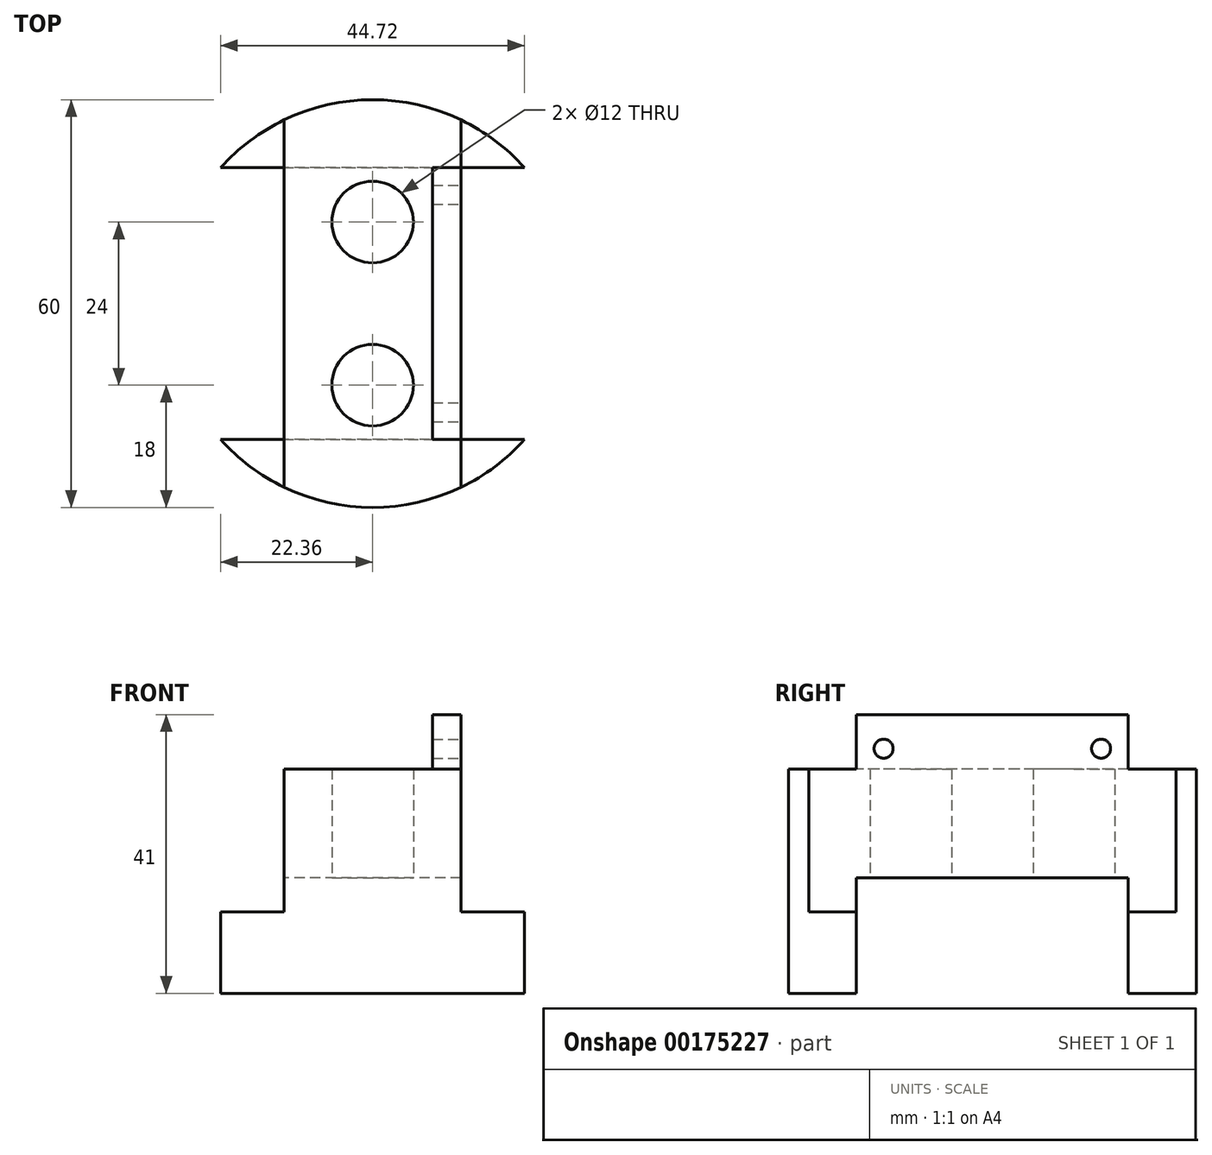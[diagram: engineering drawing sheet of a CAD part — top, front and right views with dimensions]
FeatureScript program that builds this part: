
annotation { "Feature Type Name" : "Feature", "Feature Type Description" : "" }
export const myFeature = defineFeature(function(context is Context, id is Id, definition is map)
    precondition{}
    {
        {
            var Q0;
            Q0=qCreatedBy(makeId("Top.planeOp"),FACE);
            var sketch = newSketch(context, id + "F0", { "sketchPlane" : qUnion([Q0])});
            skLineSegment(sketch, "E0.bottom", {"start": v(-13, -12) * mm, "end": v(13, -12) * mm});
            skLineSegment(sketch, "E0.top", {"start": v(-13, 12) * mm, "end": v(13, 12) * mm});
            skLineSegment(sketch, "E0.left", {"start": v(-13, -12) * mm, "end": v(-13, 12) * mm});
            skLineSegment(sketch, "E0.right", {"start": v(13, -12) * mm, "end": v(13, 12) * mm});
            skPoint(sketch, "E0.middle", {"position": v(0, 0) * mm});
            skCircle(sketch, "E1", {"center": v(0, 0) * mm, "radius": 20 * mm, "construction": true});
            skLineSegment(sketch, "E2", {"start": v(-31.1, 0) * mm, "end": v(39.02, 0) * mm, "construction": true});
            skCircle(sketch, "E3", {"center": v(0, 0) * mm, "radius": 30 * mm});
            skCircle(sketch, "E4", {"center": v(0, 12) * mm, "radius": 6 * mm});
            skCircle(sketch, "E5", {"center": v(0, -12) * mm, "radius": 6 * mm});
            skLineSegment(sketch, "E6.bottom", {"start": v(-13, 27.04) * mm, "end": v(13, 27.04) * mm});
            skLineSegment(sketch, "E6.top", {"start": v(-13, -27.04) * mm, "end": v(13, -27.04) * mm});
            skLineSegment(sketch, "E6.left", {"start": v(-13, 27.04) * mm, "end": v(-13, -27.04) * mm});
            skLineSegment(sketch, "E6.right", {"start": v(13, 27.04) * mm, "end": v(13, -27.04) * mm});
            skSolve(sketch);
        }
        {
            var Q0;
            {var subQ0=sQuery(id+"F0.wireOp",EDGE,"E6.bottom");Q0=makeQuery(id+"F0.imprint","IMPRINT",FACE,{"disambiguationData":[TD([[makeQuery(id+"F0.imprint","IMPRINT",EDGE,{"derivedFrom":subQ0}),1.0]])]});}
            var Q1;
            {var subQ0=sQuery(id+"F0.wireOp",EDGE,"E6.top");Q1=makeQuery(id+"F0.imprint","IMPRINT",FACE,{"disambiguationData":[TD([[makeQuery(id+"F0.imprint","IMPRINT",EDGE,{"derivedFrom":subQ0}),-1.0]])]});}
            var Q2;
            {var subQ0=sQuery(id+"F0.wireOp",EDGE,"E6.top");Q2=makeQuery(id+"F0.imprint","IMPRINT",FACE,{"disambiguationData":[TD([[makeQuery(id+"F0.imprint","IMPRINT",EDGE,{"derivedFrom":subQ0}),1.0]])]});}
            var Q3;
            {var subQ6=sQuery(id+"F0.wireOp",EDGE,"E0.bottom");var subQ9=sQuery(id+"F0.wireOp",EDGE,"E6.left");var subQ13=makeQuery(id+"F0.imprint","INTERSECT",VERTEX,{"derivedFrom":[subQ6,subQ9]});Q3=makeQuery(id+"F0.imprint","IMPRINT",FACE,{"disambiguationData":[TD([[makeQuery(id+"F0.imprint","IMPRINT",EDGE,{"disambiguationData":[TD([[subQ13,-1.0]])],"derivedFrom":subQ6}),1.0]])]});}
            var Q4;
            {var subQ0=sQuery(id+"F0.wireOp",EDGE,"E6.bottom");Q4=makeQuery(id+"F0.imprint","IMPRINT",FACE,{"disambiguationData":[TD([[makeQuery(id+"F0.imprint","IMPRINT",EDGE,{"derivedFrom":subQ0}),-1.0]])]});}
            extrude(context, id + "F1", {"entities" : qUnion([Q0, Q1, Q2, Q3, Q4]), "depth" : 33 * mm});
        }
        {
            var Q0;
            Q0=qCreatedBy(makeId("Top.planeOp"),FACE);
            var sketch = newSketch(context, id + "F2", { "sketchPlane" : qUnion([Q0])});
            skCircle(sketch, "E7", {"center": v(0, 0) * mm, "radius": 30 * mm});
            skCircle(sketch, "E8", {"center": v(-26.68, -13.72) * mm, "radius": 7.63 * mm});
            skLineSegment(sketch, "E9", {"start": v(-22.36, -20) * mm, "end": v(-12.88, -20) * mm});
            skLineSegment(sketch, "E10", {"start": v(-12.88, -20) * mm, "end": v(22.36, -20) * mm});
            skLineSegment(sketch, "E11", {"start": v(22.36, -20) * mm, "end": v(-53.5, 0) * mm, "construction": true});
            skLineSegment(sketch, "E12", {"start": v(-53.5, 0) * mm, "end": v(57.64, 0) * mm, "construction": true});
            skLineSegment(sketch, "E13.MirrorCS", {"start": v(-12.88, 20) * mm, "end": v(22.36, 20) * mm});
            skLineSegment(sketch, "E14.MirrorCS", {"start": v(-22.36, 20) * mm, "end": v(-12.88, 20) * mm});
            skSolve(sketch);
        }
        {
            var Q0;
            {var subQ0=sQuery(id+"F2.wireOp",EDGE,"E13.MirrorCS");Q0=makeQuery(id+"F2.imprint","IMPRINT",FACE,{"disambiguationData":[TD([[makeQuery(id+"F2.imprint","IMPRINT",EDGE,{"derivedFrom":subQ0}),1.0]])]});}
            var Q1;
            {var subQ0=sQuery(id+"F2.wireOp",EDGE,"E9");Q1=makeQuery(id+"F2.imprint","IMPRINT",FACE,{"disambiguationData":[TD([[makeQuery(id+"F2.imprint","IMPRINT",EDGE,{"derivedFrom":subQ0}),-1.0]])]});}
            extrude(context, id + "F3", {"entities" : qUnion([Q0, Q1]), "operationType" : NewBodyOperationType.ADD, "depth" : 12 * mm});
        }
        {
            var Q0;
            Q0=makeQuery(id+"F1.opExtrude","CAP_FACE",FACE,{"disambiguationData":[OSD([sQuery(id+"F0.wireOp",EDGE,"E3"),sQuery(id+"F0.wireOp",EDGE,"E4"),sQuery(id+"F0.wireOp",EDGE,"E5"),sQuery(id+"F0.wireOp",EDGE,"E6.left"),sQuery(id+"F0.wireOp",EDGE,"E6.right")])],"isStart":false});
            var sketch = newSketch(context, id + "F4", { "sketchPlane" : qUnion([Q0])});
            skLineSegment(sketch, "E15", {"start": v(0, 35.89) * mm, "end": v(0, -37.95) * mm});
            skPoint(sketch, "E15.endSnap0", {"position": v(0, 30) * mm});
            skLineSegment(sketch, "E16", {"start": v(0, -37.95) * mm, "end": v(28.6, -37.95) * mm});
            skLineSegment(sketch, "E17", {"start": v(28.6, -37.95) * mm, "end": v(28.6, 36.6) * mm});
            skLineSegment(sketch, "E18", {"start": v(28.6, 36.6) * mm, "end": v(0, 36.6) * mm});
            skLineSegment(sketch, "E19", {"start": v(0, 36.6) * mm, "end": v(0, 33.04) * mm});
            skSolve(sketch);
        }
        {
            var Q0;
            Q0=makeQuery(id+"F1.opExtrude","SWEPT_FACE",FACE,{"disambiguationData":[OSD([sQuery(id+"F0.wireOp",EDGE,"E6.left")])]});
            var sketch = newSketch(context, id + "F5", { "sketchPlane" : qUnion([Q0])});
            skLineSegment(sketch, "E20.bottom", {"start": v(-20, 0) * mm, "end": v(20, 0) * mm});
            skLineSegment(sketch, "E20.top", {"start": v(-20, 17) * mm, "end": v(20, 17) * mm});
            skLineSegment(sketch, "E20.left", {"start": v(-20, 0) * mm, "end": v(-20, 17) * mm});
            skLineSegment(sketch, "E20.right", {"start": v(20, 0) * mm, "end": v(20, 17) * mm});
            skSolve(sketch);
        }
        {
            var Q0;
            {var subQ5=sQuery(id+"F5.wireOp",EDGE,"E20.bottom");Q0=makeQuery(id+"F5.imprint","IMPRINT",FACE,{"disambiguationData":[TD([[makeQuery(id+"F5.imprint","IMPRINT",EDGE,{"derivedFrom":subQ5}),1.0]])]});}
            extrude(context, id + "F6", {"entities" : qUnion([Q0]), "operationType" : NewBodyOperationType.REMOVE, "endBound" : BoundingType.THROUGH_ALL, "oppositeDirection" : true, "depth" : 25 * mm});
        }
        {
            var Q0;
            Q0=makeQuery(id+"F6.boolean.opBoolean","COPY",FACE,{"derivedFrom":makeQuery(id+"F6.opExtrude","SWEPT_FACE",FACE,{"disambiguationData":[OSD([sQuery(id+"F5.wireOp",EDGE,"E20.top")])]})});
            var sketch = newSketch(context, id + "F7", { "sketchPlane" : qUnion([Q0])});
            skCircle(sketch, "E21", {"center": v(0, 12) * mm, "radius": 11.29 * mm, "construction": true});
            skCircle(sketch, "E22", {"center": v(0, -12) * mm, "radius": 11.29 * mm, "construction": true});
            skCircle(sketch, "E23", {"center": v(0, 12) * mm, "radius": 11.29 * mm});
            skCircle(sketch, "E24", {"center": v(0, -12) * mm, "radius": 11.29 * mm});
            skSolve(sketch);
        }
        {
            var Q0;
            Q0=makeQuery(id+"F7.imprint","IMPRINT",FACE,{"disambiguationData":[TD([[makeQuery(id+"F7.imprint","IMPRINT",EDGE,{"derivedFrom":makeQuery(id+"F6.boolean.opBoolean","INTERSECT",EDGE,{"derivedFrom":[makeQuery(id+"F1.opExtrude","SWEPT_FACE",FACE,{"disambiguationData":[OSD([sQuery(id+"F0.wireOp",EDGE,"E4")])]}),makeQuery(id+"F6.opExtrude","SWEPT_FACE",FACE,{"disambiguationData":[OSD([sQuery(id+"F5.wireOp",EDGE,"E20.top")])]})]})}),1.0]])]});
            var Q1;
            Q1=makeQuery(id+"F7.imprint","IMPRINT",FACE,{"disambiguationData":[TD([[makeQuery(id+"F7.imprint","IMPRINT",EDGE,{"derivedFrom":makeQuery(id+"F6.boolean.opBoolean","INTERSECT",EDGE,{"derivedFrom":[makeQuery(id+"F1.opExtrude","SWEPT_FACE",FACE,{"disambiguationData":[OSD([sQuery(id+"F0.wireOp",EDGE,"E5")])]}),makeQuery(id+"F6.opExtrude","SWEPT_FACE",FACE,{"disambiguationData":[OSD([sQuery(id+"F5.wireOp",EDGE,"E20.top")])]})]})}),1.0]])]});
            var Q2;
            {var subQ0=sQuery(id+"F7.wireOp",EDGE,"E23");var subQ1=makeQuery(id+"F6.boolean.opBoolean","COPY",EDGE,{"derivedFrom":makeQuery(id+"F6.opExtrude","SWEPT_EDGE",EDGE,{"disambiguationData":[OSD([sQuery(id+"F5.wireOp",EDGE,"E20.top"),sQuery(id+"F5.wireOp",EDGE,"E20.right")])]})});var subQ2=makeQuery(id+"F7.imprint","INTERSECT",VERTEX,{"disambiguationData":[OD(0.0)],"derivedFrom":[subQ1,subQ0]});Q2=makeQuery(id+"F7.imprint","IMPRINT",FACE,{"disambiguationData":[TD([[makeQuery(id+"F7.imprint","IMPRINT",EDGE,{"disambiguationData":[TD([[subQ2,1.0]])],"derivedFrom":subQ0}),1.0]])]});}
            var Q3;
            {var subQ0=sQuery(id+"F7.wireOp",EDGE,"E24");var subQ1=makeQuery(id+"F6.boolean.opBoolean","COPY",EDGE,{"derivedFrom":makeQuery(id+"F6.opExtrude","SWEPT_EDGE",EDGE,{"disambiguationData":[OSD([sQuery(id+"F5.wireOp",EDGE,"E20.top"),sQuery(id+"F5.wireOp",EDGE,"E20.left")])]})});var subQ2=makeQuery(id+"F7.imprint","INTERSECT",VERTEX,{"disambiguationData":[OD(0.0)],"derivedFrom":[subQ1,subQ0]});Q3=makeQuery(id+"F7.imprint","IMPRINT",FACE,{"disambiguationData":[TD([[makeQuery(id+"F7.imprint","IMPRINT",EDGE,{"disambiguationData":[TD([[subQ2,-1.0]])],"derivedFrom":subQ0}),1.0]])]});}
            var Q4;
            {var subQ1=sQuery(id+"F5.wireOp",EDGE,"E20.top");Q4=makeQuery(id+"F7.imprint","IMPRINT",FACE,{"disambiguationData":[TD([[makeQuery(id+"F7.imprint","IMPRINT",EDGE,{"derivedFrom":makeQuery(id+"F6.boolean.opBoolean","INTERSECT",EDGE,{"derivedFrom":[makeQuery(id+"F1.opExtrude","SWEPT_FACE",FACE,{"disambiguationData":[OSD([sQuery(id+"F0.wireOp",EDGE,"E5")])]}),makeQuery(id+"F6.opExtrude","SWEPT_FACE",FACE,{"disambiguationData":[OSD([subQ1])]})]})}),-1.0]])]});}
            extrude(context, id + "F8", {"entities" : qUnion([Q0, Q1, Q2, Q3, Q4]), "operationType" : NewBodyOperationType.REMOVE, "endBound" : BoundingType.THROUGH_ALL, "depth" : 25 * mm});
        }
        {
            var Q0;
            {var subQ0=sQuery(id+"F0.wireOp",EDGE,"E6.right");var subQ1=makeQuery(id+"F1.opExtrude","CAP_EDGE",EDGE,{"disambiguationData":[OSD([subQ0])],"isStart":false});Q0=makeQuery(id+"F4.imprint","IMPRINT",FACE,{"disambiguationData":[TD([[makeQuery(id+"F4.imprint","IMPRINT",EDGE,{"derivedFrom":subQ1}),-1.0]])]});}
            var sketch = newSketch(context, id + "F9", { "sketchPlane" : qUnion([Q0])});
            skLineSegment(sketch, "E25.bottom", {"start": v(13, 20) * mm, "end": v(-13, 20) * mm});
            skLineSegment(sketch, "E25.top", {"start": v(13, -20) * mm, "end": v(-13, -20) * mm});
            skLineSegment(sketch, "E25.left", {"start": v(13, 20) * mm, "end": v(13, -20) * mm});
            skLineSegment(sketch, "E25.right", {"start": v(-13, 20) * mm, "end": v(-13, -20) * mm});
            skPoint(sketch, "E25.middle", {"position": v(0, 0) * mm});
            skLineSegment(sketch, "E26.bottom", {"start": v(8.83, 20) * mm, "end": v(17.17, 20) * mm});
            skLineSegment(sketch, "E26.top", {"start": v(8.83, -20) * mm, "end": v(17.17, -20) * mm});
            skLineSegment(sketch, "E26.left", {"start": v(8.83, 20) * mm, "end": v(8.83, -20) * mm});
            skLineSegment(sketch, "E26.right", {"start": v(17.17, 20) * mm, "end": v(17.17, -20) * mm});
            skPoint(sketch, "E26.middle", {"position": v(13, 0) * mm});
            skSolve(sketch);
        }
        {
            var Q0;
            {var subQ0=sQuery(id+"F9.wireOp",EDGE,"E26.left");Q0=makeQuery(id+"F9.imprint","IMPRINT",FACE,{"disambiguationData":[TD([[makeQuery(id+"F9.imprint","IMPRINT",EDGE,{"derivedFrom":subQ0}),1.0]])]});}
            extrude(context, id + "F10", {"entities" : qUnion([Q0]), "operationType" : NewBodyOperationType.ADD, "depth" : 8 * mm});
        }
        {
            var Q0;
            {var subQ0=sQuery(id+"F0.wireOp",EDGE,"E6.right");Q0=makeQuery(id+"F10.boolean.opBoolean","MERGE",FACE,{"derivedFrom":[makeQuery(id+"F1.opExtrude","SWEPT_FACE",FACE,{"disambiguationData":[OSD([subQ0])]}),makeQuery(id+"F10.opExtrude","SWEPT_FACE",FACE,{"disambiguationData":[OSD([subQ0])]})]});}
            var sketch = newSketch(context, id + "F11", { "sketchPlane" : qUnion([Q0])});
            skLineSegment(sketch, "E27.bottom", {"start": v(-20, 41) * mm, "end": v(20, 41) * mm});
            skLineSegment(sketch, "E27.top", {"start": v(-20, 0) * mm, "end": v(20, 0) * mm});
            skLineSegment(sketch, "E27.left", {"start": v(-20, 41) * mm, "end": v(-20, 0) * mm});
            skLineSegment(sketch, "E27.right", {"start": v(20, 41) * mm, "end": v(20, 0) * mm});
            skLineSegment(sketch, "E28", {"start": v(-20, 36) * mm, "end": v(20, 36) * mm, "construction": true});
            skCircle(sketch, "E29", {"center": v(-16, 36) * mm, "radius": 1.4 * mm});
            skCircle(sketch, "E30", {"center": v(16, 36) * mm, "radius": 1.4 * mm});
            skSolve(sketch);
        }
        {
            var Q0;
            Q0=makeQuery(id+"F11.imprint","IMPRINT",FACE,{"disambiguationData":[TD([[makeQuery(id+"F11.imprint","IMPRINT",EDGE,{"derivedFrom":sQuery(id+"F11.wireOp",EDGE,"E29")}),1.0]])]});
            var Q1;
            Q1=makeQuery(id+"F11.imprint","IMPRINT",FACE,{"disambiguationData":[TD([[makeQuery(id+"F11.imprint","IMPRINT",EDGE,{"derivedFrom":sQuery(id+"F11.wireOp",EDGE,"E30")}),1.0]])]});
            extrude(context, id + "F12", {"entities" : qUnion([Q0, Q1]), "operationType" : NewBodyOperationType.REMOVE, "endBound" : BoundingType.THROUGH_ALL, "oppositeDirection" : true, "depth" : 25 * mm});
        }
    });
